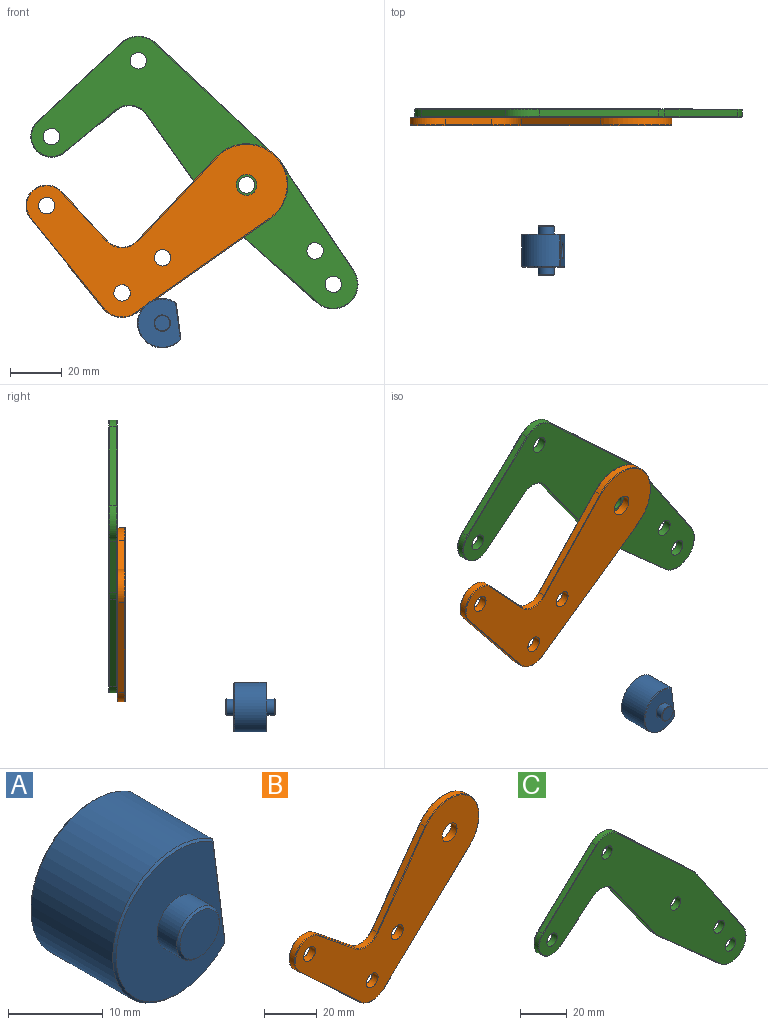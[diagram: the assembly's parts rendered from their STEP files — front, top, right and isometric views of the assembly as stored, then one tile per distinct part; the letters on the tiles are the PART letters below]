
ASSEMBLY  parts=3 mates=1
PART A: 22 faces, bbox 16.7x19.1x19.1 mm
  f0: cylinder r=9.53mm len=19.05mm, axis (0,-1,0), area 531.5mm2, adj f5,f6,f7,f15
  f1: plane 13.85x12.19mm, normal (0.99,0,0.13), area 138.7mm2, adj f5,f7,f10,f18,f20
  f2: cylinder r=3.17mm len=6.35mm, axis (0,-1,0), area 58.3mm2, adj f3,f11
  f3: plane 18.54x16.21mm, normal (0,-1,0), area 207.6mm2, adj f2,f6,f10
  f4: plane 5.84x5.84mm, normal (0,-1,0), area 26.8mm2, adj f11
  f5: plane 12.19x0.2mm, normal (0.96,0,-0.29), area 2.6mm2, adj f0,f1,f8,f16
  f6: cone r=9.27mm half-angle=45deg, axis (0,1,0), area 15.5mm2, adj f0,f3,f8,f9
  f7: plane 12.19x0.18mm, normal (0.85,0,0.53), area 2.6mm2, adj f0,f1,f9,f17
  f8: plane 0.25x0.25mm, normal (0.71,-0.67,-0.22), area 0mm2, adj f5,f6,f10
  f9: plane 0.25x0.25mm, normal (0.63,-0.67,0.39), area 0mm2, adj f6,f7,f10
  f10: plane 13.89x2.05mm, normal (0.7,-0.71,0.09), area 5mm2, adj f1,f3,f8,f9
  f11: cone r=2.92mm half-angle=45deg, axis (0,1,0), area 6.9mm2, adj f2,f4
  f12: cylinder r=3.17mm len=6.35mm, axis (0,1,0), area 58.3mm2, adj f13,f19
  f13: plane 18.54x16.21mm, normal (0,1,0), area 207.6mm2, adj f12,f15,f18
  f14: plane 5.84x5.84mm, normal (0,1,0), area 26.8mm2, adj f19
  f15: cone r=9.27mm half-angle=45deg, axis (0,-1,0), area 15.5mm2, adj f0,f13,f16,f17
  f16: plane 0.25x0.25mm, normal (0.71,0.67,-0.22), area 0mm2, adj f5,f15,f18
  f17: plane 0.25x0.25mm, normal (0.63,0.67,0.39), area 0mm2, adj f7,f15,f18
  f18: plane 13.89x2.05mm, normal (0.7,0.71,0.09), area 5mm2, adj f1,f13,f16,f17
  f19: cone r=2.92mm half-angle=45deg, axis (0,-1,0), area 6.9mm2, adj f12,f14
  f20: cylinder r=3.17mm len=13.41mm, axis (0.99,0,0.13), area 253.4mm2, adj f1,f21
  f21: plane 6.35x6.3mm, normal (0.99,0,0.13), area 31.7mm2, adj f20
PART B: 30 faces, bbox 100.9x3.2x75.5 mm
  f0: plane 45.93x43.38mm, normal (0.69,0,-0.73), area 168.5mm2, adj f1,f10,f18,f26
  f1: cylinder r=15.88mm len=28.85mm, axis (0,-1,0), area 141.5mm2, adj f0,f2,f16,f24
  f2: plane 36.43x25.66mm, normal (-0.82,0,0.58), area 118.8mm2, adj f1,f3,f14,f22
  f3: cylinder r=7.94mm len=11.47mm, axis (0,-1,0), area 34.6mm2, adj f2,f4,f15,f23
  f4: plane 20.09x16.18mm, normal (0.63,0,0.78), area 68.8mm2, adj f3,f5,f17,f25
  f5: cylinder r=7.94mm len=13.75mm, axis (0,-1,0), area 65mm2, adj f4,f6,f19,f27
  f6: plane 32.52x30.26mm, normal (-0.68,0,-0.73), area 118.5mm2, adj f5,f10,f21,f29
  f7: cylinder r=3.17mm len=6.35mm, axis (0,-1,0), area 63.3mm2, adj f12,f13
  f8: cylinder r=3.97mm len=7.94mm, axis (0,-1,0), area 79.2mm2, adj f12,f13
  f9: cylinder r=3.17mm len=6.35mm, axis (0,-1,0), area 63.3mm2, adj f12,f13
  f10: cylinder r=9.53mm len=13.03mm, axis (0,-1,0), area 38.3mm2, adj f0,f6,f20,f28
  f11: cylinder r=3.17mm len=6.35mm, axis (0,-1,0), area 63.3mm2, adj f12,f13
  f12: plane 98.48x72.89mm, normal (0,1,0), area 2669.5mm2, adj f7,f8,f9,f11,f22,f23,f24,f25
  f13: plane 98.48x72.89mm, normal (0,-1,0), area 2669.5mm2, adj f7,f8,f9,f11,f14,f15,f16,f17
  f14: cylinder r=0.25mm len=36.57mm, axis (-0.58,0,-0.82), area 17.8mm2, adj f2,f13,f15,f16
  f15: torus R=8.19mm, axis (0,-1,0), area 5.2mm2, adj f3,f13,f14,f17
  f16: torus R=15.62mm, axis (0,-1,0), area 21mm2, adj f1,f13,f14,f18
  f17: cylinder r=0.25mm len=20.25mm, axis (-0.78,0,0.63), area 10.3mm2, adj f4,f13,f15,f19
  f18: cylinder r=0.25mm len=46.11mm, axis (0.73,0,0.69), area 25.2mm2, adj f0,f13,f16,f20
  f19: torus R=7.68mm, axis (0,-1,0), area 9.6mm2, adj f5,f13,f17,f21
  f20: torus R=9.27mm, axis (0,-1,0), area 5.7mm2, adj f10,f13,f18,f21
  f21: cylinder r=0.25mm len=32.69mm, axis (0.73,0,-0.68), area 17.7mm2, adj f6,f13,f19,f20
  f22: cylinder r=0.25mm len=36.57mm, axis (0.58,0,0.82), area 17.8mm2, adj f2,f12,f23,f24
  f23: torus R=8.19mm, axis (0,-1,0), area 5.2mm2, adj f3,f12,f22,f25
  f24: torus R=15.62mm, axis (0,-1,0), area 21mm2, adj f1,f12,f22,f26
  f25: cylinder r=0.25mm len=20.25mm, axis (0.78,0,-0.63), area 10.3mm2, adj f4,f12,f23,f27
  f26: cylinder r=0.25mm len=46.11mm, axis (-0.73,0,-0.69), area 25.2mm2, adj f0,f12,f24,f28
  f27: torus R=7.68mm, axis (0,-1,0), area 9.6mm2, adj f5,f12,f25,f29
  f28: torus R=9.27mm, axis (0,-1,0), area 5.7mm2, adj f10,f12,f26,f29
  f29: cylinder r=0.25mm len=32.69mm, axis (-0.73,0,0.68), area 17.7mm2, adj f6,f12,f27,f28
PART C: 43 faces, bbox 127.5x3.2x106.7 mm
  f0: cylinder r=7.94mm len=13.73mm, axis (0,1,0), area 65mm2, adj f1,f14,f20,f32
  f1: plane 20.03x16.26mm, normal (0.63,0,-0.78), area 68.8mm2, adj f0,f2,f22,f34
  f2: cylinder r=7.94mm len=11.47mm, axis (0,1,0), area 34.6mm2, adj f1,f3,f24,f36
  f3: plane 36.33x25.79mm, normal (-0.82,0,-0.58), area 118.8mm2, adj f2,f4,f26,f38
  f4: cylinder r=15.88mm len=2.67mm, axis (0,1,0), area 9.5mm2, adj f3,f5,f28,f40
  f5: plane 37.62x33.54mm, normal (-0.67,0,-0.75), area 134.4mm2, adj f4,f6,f30,f42
  f6: cylinder r=9.53mm len=15.86mm, axis (0,1,0), area 73.4mm2, adj f5,f7,f29,f41
  f7: plane 41.82x28.13mm, normal (0.83,0,0.56), area 134.4mm2, adj f6,f8,f27,f39
  f8: cylinder r=15.88mm len=2.72mm, axis (0,1,0), area 9.5mm2, adj f7,f9,f25,f37
  f9: plane 46.09x43.21mm, normal (0.68,0,0.73), area 168.5mm2, adj f8,f10,f23,f35
  f10: cylinder r=9.53mm len=13.03mm, axis (0,1,0), area 38.3mm2, adj f9,f14,f21,f33
  f11: cylinder r=3.17mm len=6.35mm, axis (0,1,0), area 63.3mm2, adj f17,f18
  f12: cylinder r=3.17mm len=6.35mm, axis (0,1,0), area 63.3mm2, adj f17,f18
  f13: cylinder r=3.17mm len=6.35mm, axis (0,1,0), area 63.3mm2, adj f17,f18
  f14: plane 32.41x30.38mm, normal (-0.68,0,0.73), area 118.5mm2, adj f0,f10,f19,f31
  f15: cylinder r=3.17mm len=6.35mm, axis (0,1,0), area 63.3mm2, adj f17,f18
  f16: cylinder r=3.17mm len=6.35mm, axis (0,1,0), area 63.3mm2, adj f17,f18
  f17: plane 125.6x104.67mm, normal (0,-1,0), area 3681.8mm2, adj f11,f12,f13,f15,f16,f31,f32,f33
  f18: plane 125.6x104.67mm, normal (0,1,0), area 3681.8mm2, adj f11,f12,f13,f15,f16,f19,f20,f21
  f19: cylinder r=0.25mm len=32.58mm, axis (-0.73,0,-0.68), area 17.7mm2, adj f14,f18,f20,f21
  f20: torus R=7.68mm, axis (0,-1,0), area 9.6mm2, adj f0,f18,f19,f22
  f21: torus R=9.27mm, axis (0,-1,0), area 5.7mm2, adj f10,f18,f19,f23
  f22: cylinder r=0.25mm len=20.19mm, axis (0.78,0,0.63), area 10.3mm2, adj f1,f18,f20,f24
  f23: cylinder r=0.25mm len=46.27mm, axis (-0.73,0,0.68), area 25.2mm2, adj f9,f18,f21,f25
  f24: torus R=8.19mm, axis (0,-1,0), area 5.2mm2, adj f2,f18,f22,f26
  f25: torus R=15.62mm, axis (0,-1,0), area 1.4mm2, adj f8,f18,f23,f27
  f26: cylinder r=0.25mm len=36.48mm, axis (0.58,0,-0.82), area 17.8mm2, adj f3,f18,f24,f28
  f27: cylinder r=0.25mm len=41.96mm, axis (-0.56,0,0.83), area 20.1mm2, adj f7,f18,f25,f29
  f28: torus R=15.62mm, axis (0,-1,0), area 1.4mm2, adj f4,f18,f26,f30
  f29: torus R=9.27mm, axis (0,-1,0), area 10.9mm2, adj f6,f18,f27,f30
  f30: cylinder r=0.25mm len=37.79mm, axis (0.75,0,-0.67), area 20.1mm2, adj f5,f18,f28,f29
  f31: cylinder r=0.25mm len=32.58mm, axis (0.73,0,0.68), area 17.7mm2, adj f14,f17,f32,f33
  f32: torus R=7.68mm, axis (0,-1,0), area 9.6mm2, adj f0,f17,f31,f34
  f33: torus R=9.27mm, axis (0,-1,0), area 5.7mm2, adj f10,f17,f31,f35
  f34: cylinder r=0.25mm len=20.19mm, axis (-0.78,0,-0.63), area 10.3mm2, adj f1,f17,f32,f36
  f35: cylinder r=0.25mm len=46.27mm, axis (0.73,0,-0.68), area 25.2mm2, adj f9,f17,f33,f37
  f36: torus R=8.19mm, axis (0,-1,0), area 5.2mm2, adj f2,f17,f34,f38
  f37: torus R=15.62mm, axis (0,-1,0), area 1.4mm2, adj f8,f17,f35,f39
  f38: cylinder r=0.25mm len=36.48mm, axis (-0.58,0,0.82), area 17.8mm2, adj f3,f17,f36,f40
  f39: cylinder r=0.25mm len=41.96mm, axis (0.56,0,-0.83), area 20.1mm2, adj f7,f17,f37,f41
  f40: torus R=15.62mm, axis (0,-1,0), area 1.4mm2, adj f4,f17,f38,f42
  f41: torus R=9.27mm, axis (0,-1,0), area 10.9mm2, adj f6,f17,f39,f42
  f42: cylinder r=0.25mm len=37.79mm, axis (-0.75,0,0.67), area 20.1mm2, adj f5,f17,f40,f41
PLACE A t=(9.06,-64,-5.27)mm
PLACE B rot(axis=(0,1,0),8.2deg) t=(0,-6.35,0)mm
PLACE C at identity fixed
MATE revolute C.f4 <-> B.f1  axis (0,1,0) through (0,-3.18,0)mm
